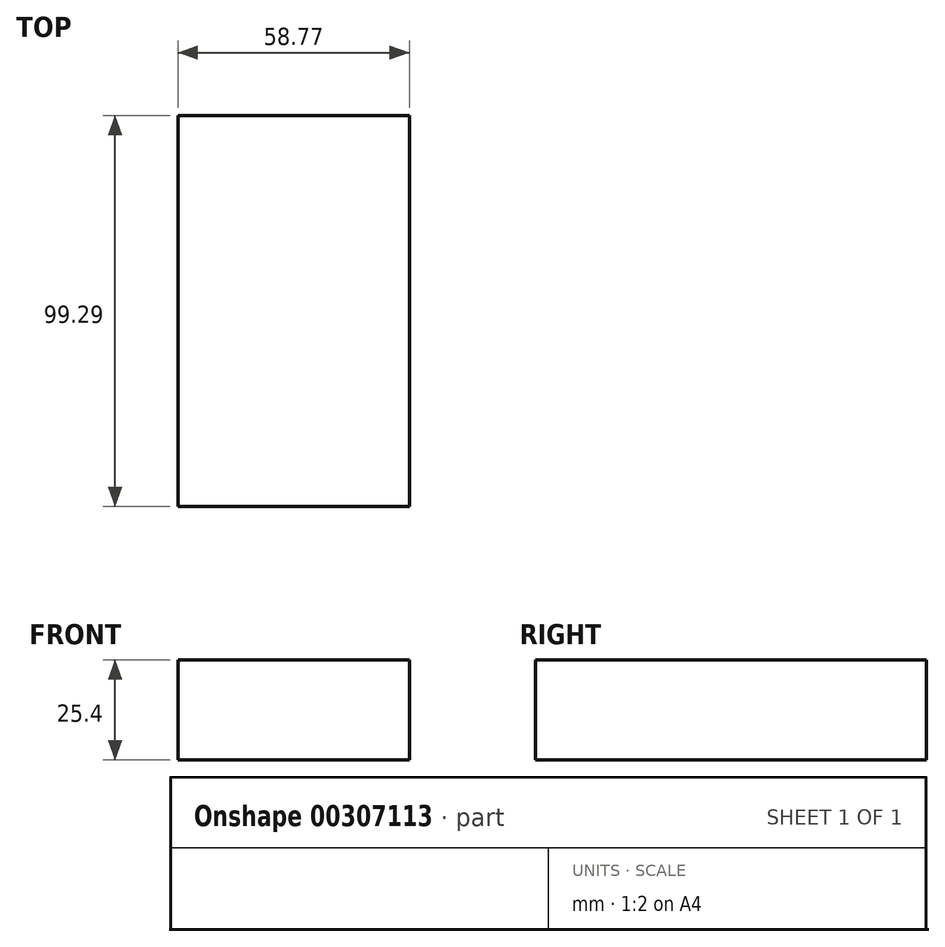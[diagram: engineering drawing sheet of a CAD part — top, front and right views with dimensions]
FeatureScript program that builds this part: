
annotation { "Feature Type Name" : "Feature", "Feature Type Description" : "" }
export const myFeature = defineFeature(function(context is Context, id is Id, definition is map)
    precondition{}
    {
        {
            var Q0;
            Q0=qCreatedBy(makeId("Top.planeOp"),FACE);
            var sketch = newSketch(context, id + "F0", { "sketchPlane" : qUnion([Q0])});
            skLineSegment(sketch, "E0.bottom", {"start": v(0, -39.79) * mm, "end": v(58.77, -39.79) * mm});
            skLineSegment(sketch, "E0.top", {"start": v(0, 59.5) * mm, "end": v(58.77, 59.5) * mm});
            skLineSegment(sketch, "E0.left", {"start": v(0, -39.79) * mm, "end": v(0, 59.5) * mm});
            skLineSegment(sketch, "E0.right", {"start": v(58.77, -39.79) * mm, "end": v(58.77, 59.5) * mm});
            skSolve(sketch);
        }
        {
            var Q0;
            Q0=makeQuery(id+"F0.imprint","IMPRINT",FACE,{"disambiguationData":[TD([[makeQuery(id+"F0.imprint","IMPRINT",EDGE,{"derivedFrom":sQuery(id+"F0.wireOp",EDGE,"E0.bottom")}),1.0]])]});
            var sketch = newSketch(context, id + "F1", { "sketchPlane" : qUnion([Q0])});
            skSolve(sketch);
        }
        {
            var Q0;
            Q0=makeQuery(id+"F1.imprint","IMPRINT",FACE,{"disambiguationData":[TD([[makeQuery(id+"F1.imprint","IMPRINT",EDGE,{"derivedFrom":makeQuery(id+"F0.imprint","IMPRINT",EDGE,{"derivedFrom":sQuery(id+"F0.wireOp",EDGE,"E0.bottom")})}),1.0]])]});
            var sketch = newSketch(context, id + "F2", { "sketchPlane" : qUnion([Q0])});
            skSolve(sketch);
        }
        {
            var Q0;
            Q0=makeQuery(id+"F1.imprint","IMPRINT",FACE,{"disambiguationData":[TD([[makeQuery(id+"F1.imprint","IMPRINT",EDGE,{"derivedFrom":makeQuery(id+"F0.imprint","IMPRINT",EDGE,{"derivedFrom":sQuery(id+"F0.wireOp",EDGE,"E0.bottom")})}),1.0]])]});
            extrude(context, id + "F3", {"entities" : qUnion([Q0]), "depth" : 25.4 * mm});
        }
        {
            var Q0;
            Q0=makeQuery(id+"F2.imprint","IMPRINT",FACE,{"disambiguationData":[TD([[makeQuery(id+"F2.imprint","IMPRINT",EDGE,{"derivedFrom":makeQuery(id+"F1.imprint","IMPRINT",EDGE,{"derivedFrom":makeQuery(id+"F0.imprint","IMPRINT",EDGE,{"derivedFrom":sQuery(id+"F0.wireOp",EDGE,"E0.bottom")})})}),1.0]])]});
            var sketch = newSketch(context, id + "F4", { "sketchPlane" : qUnion([Q0])});
            skLineSegment(sketch, "E1.bottom", {"start": v(47.05, -29.3) * mm, "end": v(4.79, -29.3) * mm});
            skLineSegment(sketch, "E1.top", {"start": v(47.05, 51.89) * mm, "end": v(4.79, 51.89) * mm});
            skLineSegment(sketch, "E1.left", {"start": v(47.05, -29.3) * mm, "end": v(47.05, 51.89) * mm});
            skLineSegment(sketch, "E1.right", {"start": v(4.79, -29.3) * mm, "end": v(4.79, 51.89) * mm});
            skSolve(sketch);
        }
        {
            var Q0;
            Q0=makeQuery(id+"F4.imprint","IMPRINT",FACE,{"disambiguationData":[TD([[makeQuery(id+"F4.imprint","IMPRINT",EDGE,{"derivedFrom":sQuery(id+"F4.wireOp",EDGE,"E1.bottom")}),-1.0]])]});
            extrude(context, id + "F5", {"entities" : qUnion([Q0]), "operationType" : NewBodyOperationType.REMOVE, "oppositeDirection" : true, "depth" : 127 * mm});
        }
        {
            var Q0;
            Q0=makeQuery(id+"F2.imprint","IMPRINT",FACE,{"disambiguationData":[TD([[makeQuery(id+"F2.imprint","IMPRINT",EDGE,{"derivedFrom":makeQuery(id+"F1.imprint","IMPRINT",EDGE,{"derivedFrom":makeQuery(id+"F0.imprint","IMPRINT",EDGE,{"derivedFrom":sQuery(id+"F0.wireOp",EDGE,"E0.bottom")})})}),1.0]])]});
            extrude(context, id + "F6", {"entities" : qUnion([Q0]), "operationType" : NewBodyOperationType.REMOVE, "oppositeDirection" : true, "depth" : 25.4 * mm});
        }
    });
